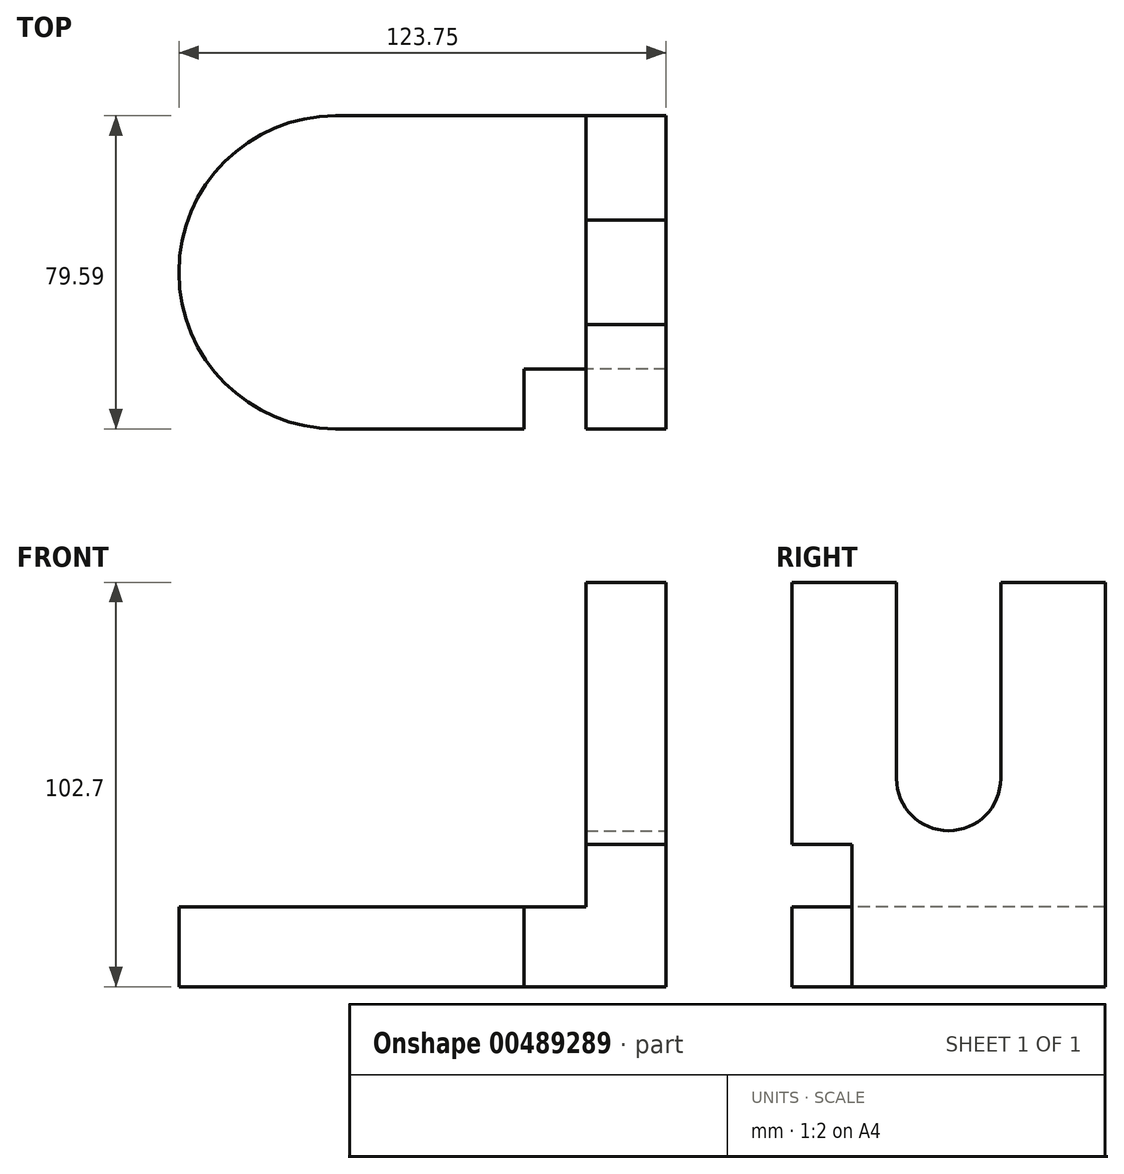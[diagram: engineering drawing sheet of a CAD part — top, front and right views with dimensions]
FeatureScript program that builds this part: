
annotation { "Feature Type Name" : "Feature", "Feature Type Description" : "" }
export const myFeature = defineFeature(function(context is Context, id is Id, definition is map)
    precondition{}
    {
        {
            var Q0;
            Q0=qCreatedBy(makeId("Right.planeOp"),FACE);
            var sketch = newSketch(context, id + "F0", { "sketchPlane" : qUnion([Q0])});
            skLineSegment(sketch, "E0.bottom", {"start": v(0, 0) * mm, "end": v(79.59, 0) * mm});
            skLineSegment(sketch, "E0.top", {"start": v(0, 102.7) * mm, "end": v(26.56, 102.7) * mm});
            skLineSegment(sketch, "E0.left", {"start": v(0, 0) * mm, "end": v(0, 102.7) * mm});
            skLineSegment(sketch, "E0.right", {"start": v(79.59, 0) * mm, "end": v(79.59, 102.7) * mm});
            skLineSegment(sketch, "E1.left", {"start": v(53.03, 102.7) * mm, "end": v(53.03, 52.85) * mm});
            skLineSegment(sketch, "E1.right", {"start": v(26.56, 102.7) * mm, "end": v(26.56, 52.85) * mm});
            skArc(sketch, "E2", {"start": v(26.56, 52.85) * mm, "mid": v(39.8, 39.62) * mm, "end": v(53.03, 52.85) * mm});
            skLineSegment(sketch, "E3.trimOffspring", {"start": v(53.03, 102.7) * mm, "end": v(79.59, 102.7) * mm});
            skSolve(sketch);
        }
        {
            var Q0;
            Q0=makeQuery(id+"F0.imprint","IMPRINT",FACE,{"disambiguationData":[TD([[makeQuery(id+"F0.imprint","IMPRINT",EDGE,{"derivedFrom":sQuery(id+"F0.wireOp",EDGE,"E0.bottom")}),1.0]])]});
            extrude(context, id + "F1", {"entities" : qUnion([Q0]), "oppositeDirection" : true, "depth" : 20.32 * mm});
        }
        {
            var Q0;
            Q0=qCreatedBy(makeId("Top.planeOp"),FACE);
            var sketch = newSketch(context, id + "F2", { "sketchPlane" : qUnion([Q0])});
            skLineSegment(sketch, "E4.bottom", {"start": v(0, 0) * mm, "end": v(-83.96, 0) * mm});
            skLineSegment(sketch, "E4.top", {"start": v(0, 79.59) * mm, "end": v(-83.96, 79.59) * mm});
            skLineSegment(sketch, "E4.left", {"start": v(0, 0) * mm, "end": v(0, 79.59) * mm});
            skArc(sketch, "E5", {"start": v(-83.96, 79.59) * mm, "mid": v(-123.75, 39.8) * mm, "end": v(-83.96, 0) * mm});
            skSolve(sketch);
        }
        {
            var Q0;
            Q0=makeQuery(id+"F2.imprint","IMPRINT",FACE,{"disambiguationData":[TD([[makeQuery(id+"F2.imprint","IMPRINT",EDGE,{"derivedFrom":sQuery(id+"F2.wireOp",EDGE,"E4.bottom")}),-1.0]])]});
            extrude(context, id + "F3", {"entities" : qUnion([Q0]), "operationType" : NewBodyOperationType.ADD, "depth" : 20.32 * mm});
        }
        {
            var Q0;
            Q0=qCreatedBy(makeId("Front.planeOp"),FACE);
            var sketch = newSketch(context, id + "F4", { "sketchPlane" : qUnion([Q0])});
            skLineSegment(sketch, "E6.bottom", {"start": v(0, 0) * mm, "end": v(-36.13, 0) * mm});
            skLineSegment(sketch, "E6.top", {"start": v(0, 36.13) * mm, "end": v(-36.13, 36.13) * mm});
            skLineSegment(sketch, "E6.left", {"start": v(0, 0) * mm, "end": v(0, 36.13) * mm});
            skLineSegment(sketch, "E6.right", {"start": v(-36.13, 0) * mm, "end": v(-36.13, 36.13) * mm});
            skSolve(sketch);
        }
        {
            var Q0;
            Q0=makeQuery(id+"F4.imprint","IMPRINT",FACE,{"disambiguationData":[TD([[makeQuery(id+"F4.imprint","IMPRINT",EDGE,{"derivedFrom":sQuery(id+"F4.wireOp",EDGE,"E6.bottom")}),-1.0]])]});
            extrude(context, id + "F5", {"entities" : qUnion([Q0]), "operationType" : NewBodyOperationType.REMOVE, "oppositeDirection" : true, "depth" : 15.24 * mm});
        }
    });
